# Revit family: Accessory-Handshower_Holder-KOHLER-RENEW-K-98348T
name_source: partatom
category: Specialty Equipment
revit_build: Autodesk Revit 2017 (Build: 20160225_1515(x64)
units: mm (PartAtom-declared; Revit-internal decimal feet)

## family parameters
Cut with Voids When Loaded = No
Host = Face
OmniClass Number = 23.31.25.00
OmniClass Title = Toilet and Bath Specialties
Part Type = Normal
Room Calculation Point = No
Round Connector Dimension = Use Diameter
Shared = No

## types (6) — shared parameters
ADA Compliant = No
Assembly Code = C1030200
Date Modified = 08/25/2020
Default Elevation = 42"
Description = Oxygen Mu adjustable shower bracket
Height = 2 1/4"
Length = 3 3/8"
Manufacturer = KOHLER Co.
Master Format 2014 = 10 28 00
Master Format 2014 Name = Toilet, Bath, and Laundry Accessories
Material = Premium Metal Construction
Product Documentation Link = https://files.kohler.com.cn
Product Name = RENEW
Product Page URL = https://www.kohler.com.cn
URL = http://www.kohler.com.cn
WaterSense Certified = No
Width = 2"

## per-type parameters (varying)
| type | Finish | Model | Type |
| CP-Polished Chrome | Kohler-Metal-CP-Polished_Chrome | K-98348T-CP | 1 |
| 2BL-Original Black | Kohler-Metal-2BL-Original_Black | K-98348T-2BL | 2 |
| AF-Flange gold | Kohler-Metal-AF-Flange_Gold | K-98348T-AF | 3 |
| BN-Roman silver | Kohler-Metal-BN-Roman_Silver | K-98348T-BN | 4 |
| RGD-Rose Gold | Kohler-Metal-RGD-Rose_Gold | K-98348T-RGD | 5 |
| BL-Matte Black | Kohler-Metal-BL-Matte_Black | K-98348T-BL | 6 |

## geometry (parser evidence)
native form markers: Sweep x6
no freeform markers — native parametric forms only
